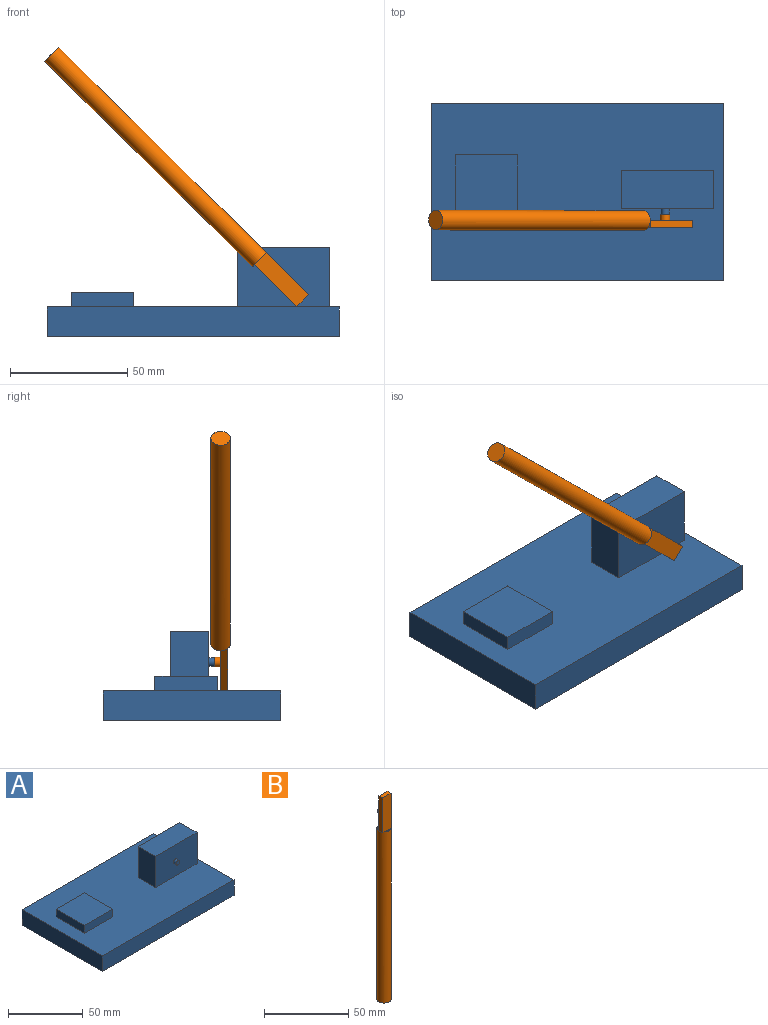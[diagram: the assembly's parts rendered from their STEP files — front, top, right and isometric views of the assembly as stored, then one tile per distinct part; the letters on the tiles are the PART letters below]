
ASSEMBLY  parts=2 mates=1
PART A: 18 faces, bbox 124.6x75.7x38.1 mm
  f0: plane 124.63x75.7mm, normal (0,0,1), area 8070.9mm2, adj f1,f2,f3,f4,f6,f7,f8,f9
  f1: plane 75.7x12.7mm, normal (-1,0,0), area 961.4mm2, adj f0,f2,f4,f5
  f2: plane 124.63x12.7mm, normal (0,-1,0), area 1582.8mm2, adj f0,f1,f3,f5
  f3: plane 75.7x12.7mm, normal (1,0,0), area 961.4mm2, adj f0,f2,f4,f5
  f4: plane 124.63x12.7mm, normal (0,1,0), area 1582.8mm2, adj f0,f1,f3,f5
  f5: plane 124.63x75.7mm, normal (0,0,-1), area 9434.8mm2, adj f1,f2,f3,f4
  f6: plane 39.33x25.4mm, normal (0,-1,0), area 988.9mm2, adj f0,f7,f9,f10,f16
  f7: plane 25.4x16.39mm, normal (1,0,0), area 416.3mm2, adj f0,f6,f8,f10
  f8: plane 39.33x25.4mm, normal (0,1,0), area 999.1mm2, adj f0,f7,f9,f10
  f9: plane 25.4x16.39mm, normal (-1,0,0), area 416.3mm2, adj f0,f6,f8,f10
  f10: plane 39.33x16.39mm, normal (0,0,1), area 644.7mm2, adj f6,f7,f8,f9
  f11: plane 26.82x6.35mm, normal (-1,0,0), area 170.3mm2, adj f0,f12,f14,f15
  f12: plane 26.82x6.35mm, normal (0,-1,0), area 170.3mm2, adj f0,f11,f13,f15
  f13: plane 26.82x6.35mm, normal (1,0,0), area 170.3mm2, adj f0,f12,f14,f15
  f14: plane 26.82x6.35mm, normal (0,1,0), area 170.3mm2, adj f0,f11,f13,f15
  f15: plane 26.82x26.82mm, normal (0,0,1), area 719.3mm2, adj f11,f12,f13,f14
  f16: cylinder r=1.8mm len=3.6mm, axis (0,1,0), area 28.7mm2, adj f6,f17
  f17: plane 3.6x3.6mm, normal (0,-1,0), area 10.2mm2, adj f16
PART B: 12 faces, bbox 8.4x8.4x150 mm
  f0: plane 8.41x7.2mm, normal (0,0,1), area 30.4mm2, adj f1,f6,f7
  f1: cylinder r=4.21mm len=124.61mm, axis (0,0,-1), area 3293.4mm2, adj f0,f2,f3,f4
  f2: plane 5.9x1.21mm, normal (0,0,1), area 4.9mm2, adj f1,f5
  f3: plane 8.41x8.41mm, normal (0,0,-1), area 55.6mm2, adj f1
  f4: plane 3x1.25mm, normal (0,0,-1), area 1.2mm2, adj f1,f5,f8
  f5: plane 25.4x7.16mm, normal (0,-1,0), area 181.8mm2, adj f2,f4,f6,f8,f9
  f6: plane 25.4x3mm, normal (1,0,0), area 76.1mm2, adj f0,f5,f7,f9
  f7: plane 25.4x7.16mm, normal (0,1,0), area 168.8mm2, adj f0,f6,f8,f9,f10
  f8: plane 25.4x3mm, normal (-1,0,0), area 76.1mm2, adj f4,f5,f7,f9
  f9: plane 7.16x3mm, normal (0,0,1), area 21.4mm2, adj f5,f6,f7,f8
  f10: cylinder r=2.04mm len=4.07mm, axis (0,-1,0), area 32.5mm2, adj f7,f11
  f11: plane 4.07x4.07mm, normal (0,1,0), area 13mm2, adj f10
PLACE A t=(-43.53,-21.95,8.53)mm
PLACE B rot(axis=(0,1,0),134.7deg) t=(-99.81,-37.61,129.01)mm
MATE revolute B.f10 <-> A.f16  axis (0,1,0) through (-1.92,-35.07,33.54)mm
